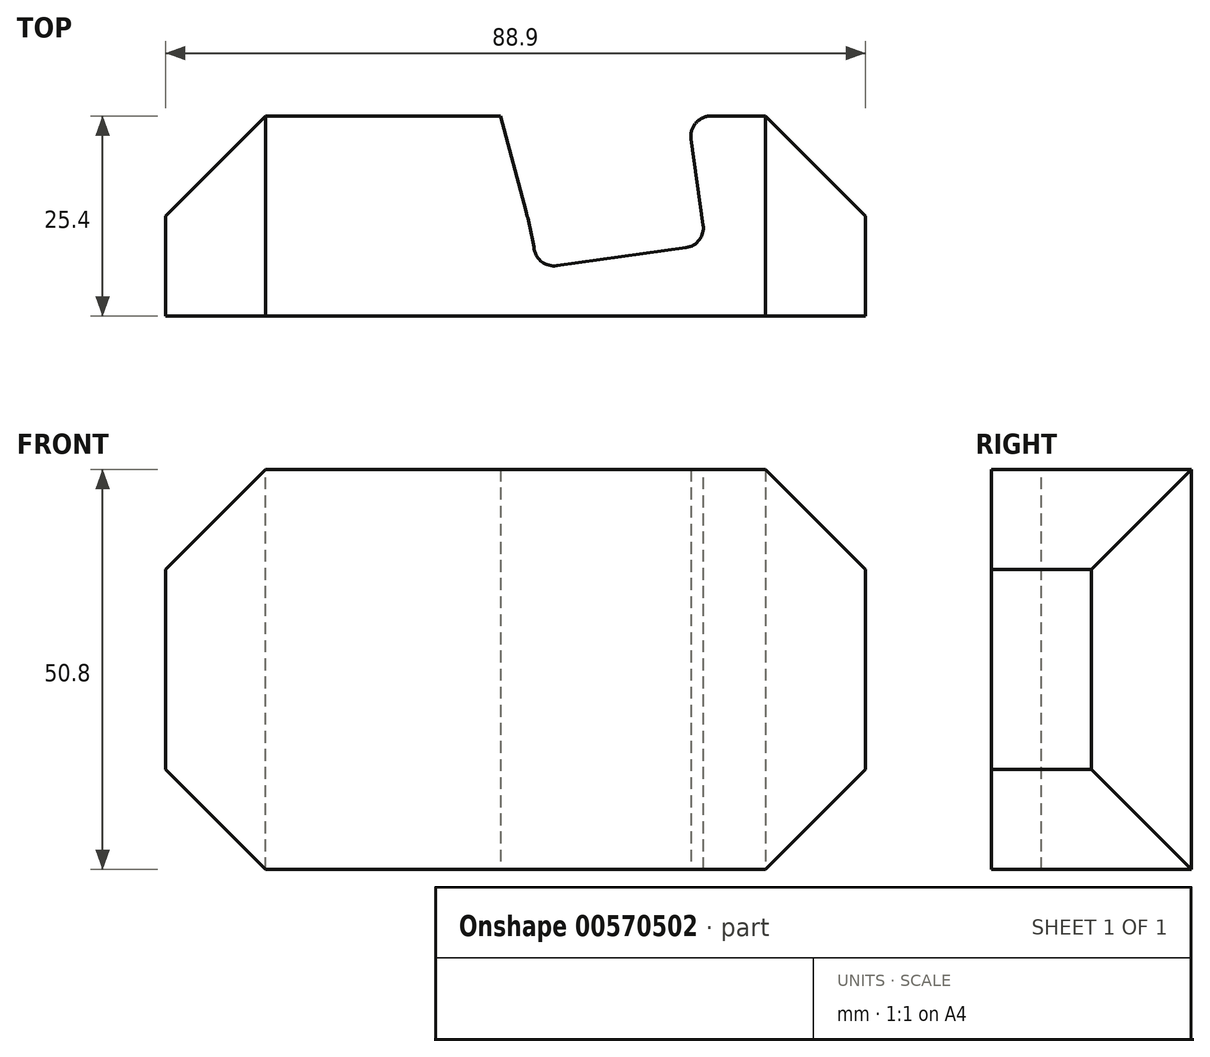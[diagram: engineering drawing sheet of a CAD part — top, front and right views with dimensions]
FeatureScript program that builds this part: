
annotation { "Feature Type Name" : "Feature", "Feature Type Description" : "" }
export const myFeature = defineFeature(function(context is Context, id is Id, definition is map)
    precondition{}
    {
        {
            var Q0;
            Q0=qCreatedBy(makeId("Top.planeOp"),FACE);
            var sketch = newSketch(context, id + "F0", { "sketchPlane" : qUnion([Q0])});
            skLineSegment(sketch, "E0.bottom", {"start": v(0, 0) * mm, "end": v(88.9, 0) * mm});
            skLineSegment(sketch, "E0.top", {"start": v(0, 25.4) * mm, "end": v(88.9, 25.4) * mm});
            skLineSegment(sketch, "E0.left", {"start": v(0, 0) * mm, "end": v(0, 25.4) * mm});
            skLineSegment(sketch, "E0.right", {"start": v(88.9, 0) * mm, "end": v(88.9, 25.4) * mm});
            skLineSegment(sketch, "E1", {"start": v(44.45, 25.4) * mm, "end": v(47.17, 6.03) * mm});
            skLineSegment(sketch, "E2", {"start": v(68.64, 9.05) * mm, "end": v(66.35, 25.4) * mm});
            skLineSegment(sketch, "E3", {"start": v(47.17, 6.03) * mm, "end": v(68.64, 9.05) * mm});
            skSolve(sketch);
        }
        {
            var Q0;
            Q0=makeQuery(id+"F0.imprint","IMPRINT",FACE,{"disambiguationData":[TD([[makeQuery(id+"F0.imprint","IMPRINT",EDGE,{"derivedFrom":sQuery(id+"F0.wireOp",EDGE,"E0.bottom")}),1.0]])]});
            extrude(context, id + "F1", {"entities" : qUnion([Q0]), "depth" : 50.8 * mm, "offsetDistance" : 25.4 * mm});
        }
        {
            var Q0;
            Q0=makeQuery(id+"F1.opExtrude","SWEPT_EDGE",EDGE,{"disambiguationData":[OSD([sQuery(id+"F0.wireOp",EDGE,"E1"),sQuery(id+"F0.wireOp",EDGE,"E3")])]});
            var Q1;
            Q1=makeQuery(id+"F1.opExtrude","SWEPT_EDGE",EDGE,{"disambiguationData":[OSD([sQuery(id+"F0.wireOp",EDGE,"E2"),sQuery(id+"F0.wireOp",EDGE,"E3")])]});
            var Q2;
            Q2=makeQuery(id+"F1.opExtrude","SWEPT_EDGE",EDGE,{"disambiguationData":[OSD([sQuery(id+"F0.wireOp",EDGE,"E0.top"),sQuery(id+"F0.wireOp",EDGE,"E2")])]});
            fillet(context, id + "F2", {"entities" : qUnion([Q0, Q1, Q2]), "radius" : 2.54 * mm, "tangentPropagation" : true, "allowEdgeOverflow" : false});
        }
        {
            var Q0;
            Q0=makeQuery(id+"F1.opExtrude","SWEPT_EDGE",EDGE,{"disambiguationData":[OSD([sQuery(id+"F0.wireOp",EDGE,"E0.top"),sQuery(id+"F0.wireOp",EDGE,"E1")])]});
            chamfer(context, id + "F3", {"entities" : qUnion([Q0]), "chamferType" : ChamferType.OFFSET_ANGLE, "width" : 1.9 * mm, "oppositeDirection" : false, "angle" : 75 * degree, "tangentPropagation" : true});
        }
        {
            var Q0;
            {var subQ0=sQuery(id+"F0.wireOp",EDGE,"E1");Q0=makeQuery(id+"F3.opChamfer","BLEND_EDGE",EDGE,{"blendedFrom":[makeQuery(id+"F1.opExtrude","SWEPT_EDGE",EDGE,{"disambiguationData":[OSD([sQuery(id+"F0.wireOp",EDGE,"E0.top"),subQ0])]}),makeQuery(id+"F1.opExtrude","SWEPT_FACE",FACE,{"disambiguationData":[OSD([subQ0])]})],"blendedInto":[makeQuery(id+"F1.opExtrude","SWEPT_FACE",FACE,{"disambiguationData":[OSD([subQ0])]})]});}
            fillet(context, id + "F4", {"entities" : qUnion([Q0]), "radius" : 50.8 * mm, "tangentPropagation" : true, "allowEdgeOverflow" : false});
        }
        {
            var Q0;
            Q0=makeQuery(id+"F1.opExtrude","SWEPT_EDGE",EDGE,{"disambiguationData":[OSD([sQuery(id+"F0.wireOp",EDGE,"E0.top"),sQuery(id+"F0.wireOp",EDGE,"E0.right")])]});
            var Q1;
            Q1=makeQuery(id+"F1.opExtrude","CAP_EDGE",EDGE,{"disambiguationData":[OSD([sQuery(id+"F0.wireOp",EDGE,"E0.right")])],"isStart":false});
            var Q2;
            Q2=makeQuery(id+"F1.opExtrude","CAP_EDGE",EDGE,{"disambiguationData":[OSD([sQuery(id+"F0.wireOp",EDGE,"E0.right")])],"isStart":true});
            var Q3;
            Q3=makeQuery(id+"F1.opExtrude","SWEPT_EDGE",EDGE,{"disambiguationData":[OSD([sQuery(id+"F0.wireOp",EDGE,"E0.top"),sQuery(id+"F0.wireOp",EDGE,"E0.left")])]});
            var Q4;
            Q4=makeQuery(id+"F1.opExtrude","CAP_EDGE",EDGE,{"disambiguationData":[OSD([sQuery(id+"F0.wireOp",EDGE,"E0.left")])],"isStart":false});
            var Q5;
            Q5=makeQuery(id+"F1.opExtrude","CAP_EDGE",EDGE,{"disambiguationData":[OSD([sQuery(id+"F0.wireOp",EDGE,"E0.left")])],"isStart":true});
            chamfer(context, id + "F5", {"entities" : qUnion([Q0, Q1, Q2, Q3, Q4, Q5]), "width" : 12.7 * mm, "tangentPropagation" : true});
        }
    });
